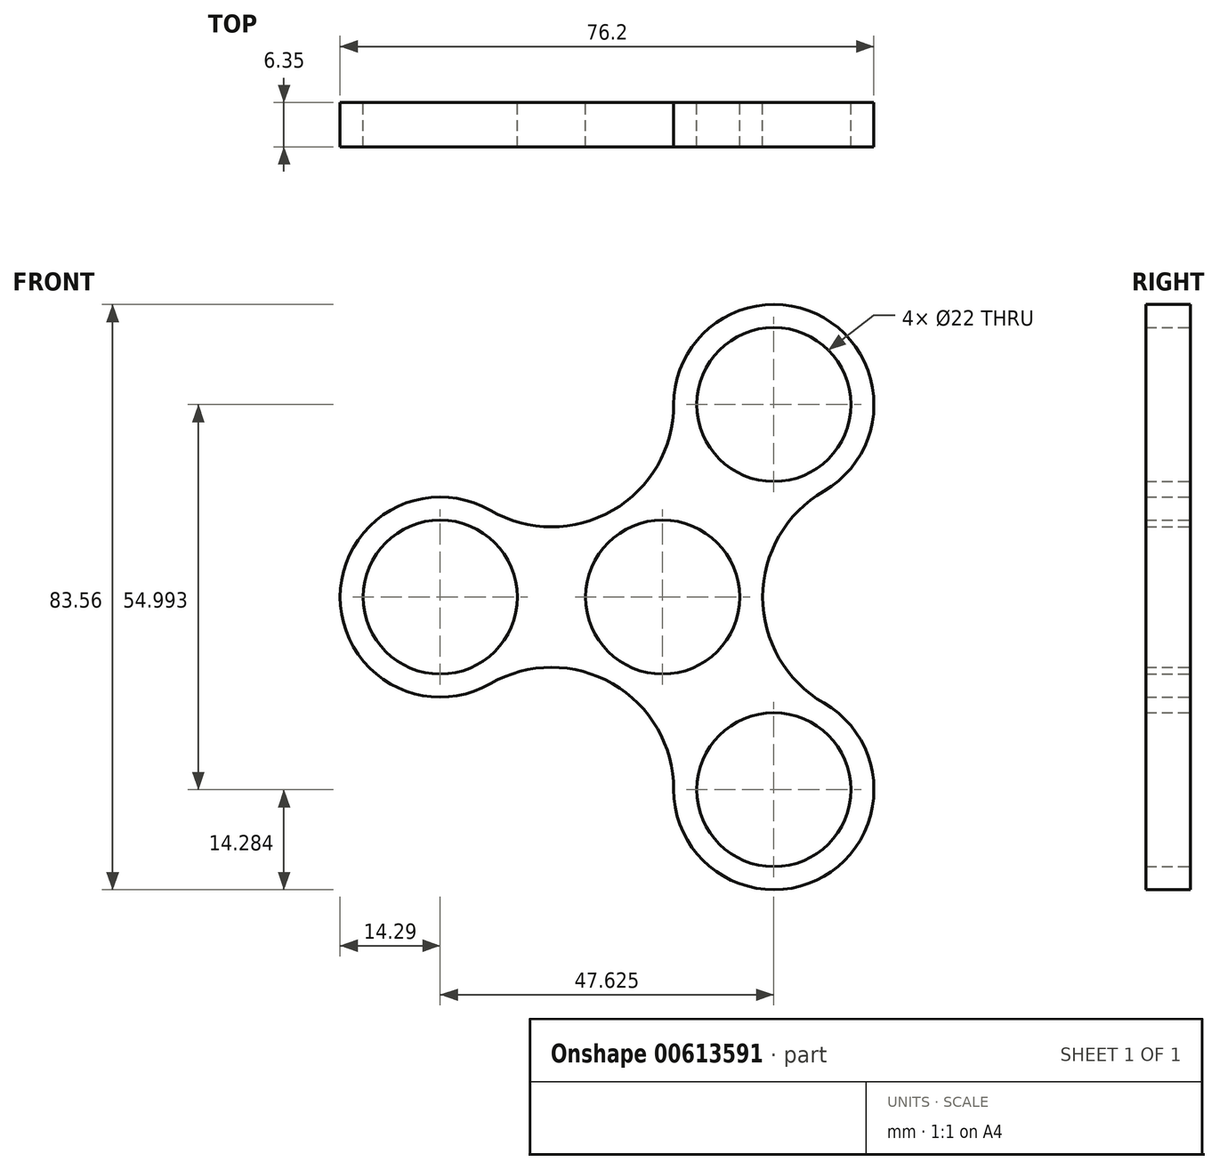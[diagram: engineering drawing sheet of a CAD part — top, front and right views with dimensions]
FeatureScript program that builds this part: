
annotation { "Feature Type Name" : "Feature", "Feature Type Description" : "" }
export const myFeature = defineFeature(function(context is Context, id is Id, definition is map)
    precondition{}
    {
        {
            var Q0;
            Q0=qCreatedBy(makeId("Front.planeOp"),FACE);
            var sketch = newSketch(context, id + "F0", { "sketchPlane" : qUnion([Q0])});
            skCircle(sketch, "E0", {"center": v(0, 0) * mm, "radius": 14.29 * mm});
            skCircle(sketch, "E1", {"center": v(0, 0) * mm, "radius": 11 * mm});
            skCircle(sketch, "E2", {"center": v(-31.75, 0) * mm, "radius": 14.29 * mm});
            skCircle(sketch, "E3", {"center": v(-31.75, 0) * mm, "radius": 11 * mm});
            skCircle(sketch, "E4.1.0", {"center": v(15.87, -27.5) * mm, "radius": 11 * mm});
            skCircle(sketch, "E4.1.1", {"center": v(15.87, -27.5) * mm, "radius": 14.29 * mm});
            skCircle(sketch, "E4.2.0", {"center": v(15.88, 27.5) * mm, "radius": 11 * mm});
            skCircle(sketch, "E4.2.1", {"center": v(15.88, 27.5) * mm, "radius": 14.29 * mm});
            skArc(sketch, "E5", {"start": v(-24.6, 12.37) * mm, "mid": v(-7.14, 12.37) * mm, "end": v(1.59, 27.5) * mm});
            skArc(sketch, "E6", {"start": v(23.02, 15.12) * mm, "mid": v(14.29, 0) * mm, "end": v(23.02, -15.12) * mm});
            skArc(sketch, "E7", {"start": v(1.59, -27.5) * mm, "mid": v(-7.14, -12.37) * mm, "end": v(-24.6, -12.37) * mm});
            skSolve(sketch);
        }
        {
            var Q0;
            Q0 = qSketchRegion(id + "F0", true);
            extrude(context, id + "F1", {"entities" : qUnion([Q0]), "depth" : 6.35 * mm, "offsetDistance" : 25.4 * mm});
        }
    });
